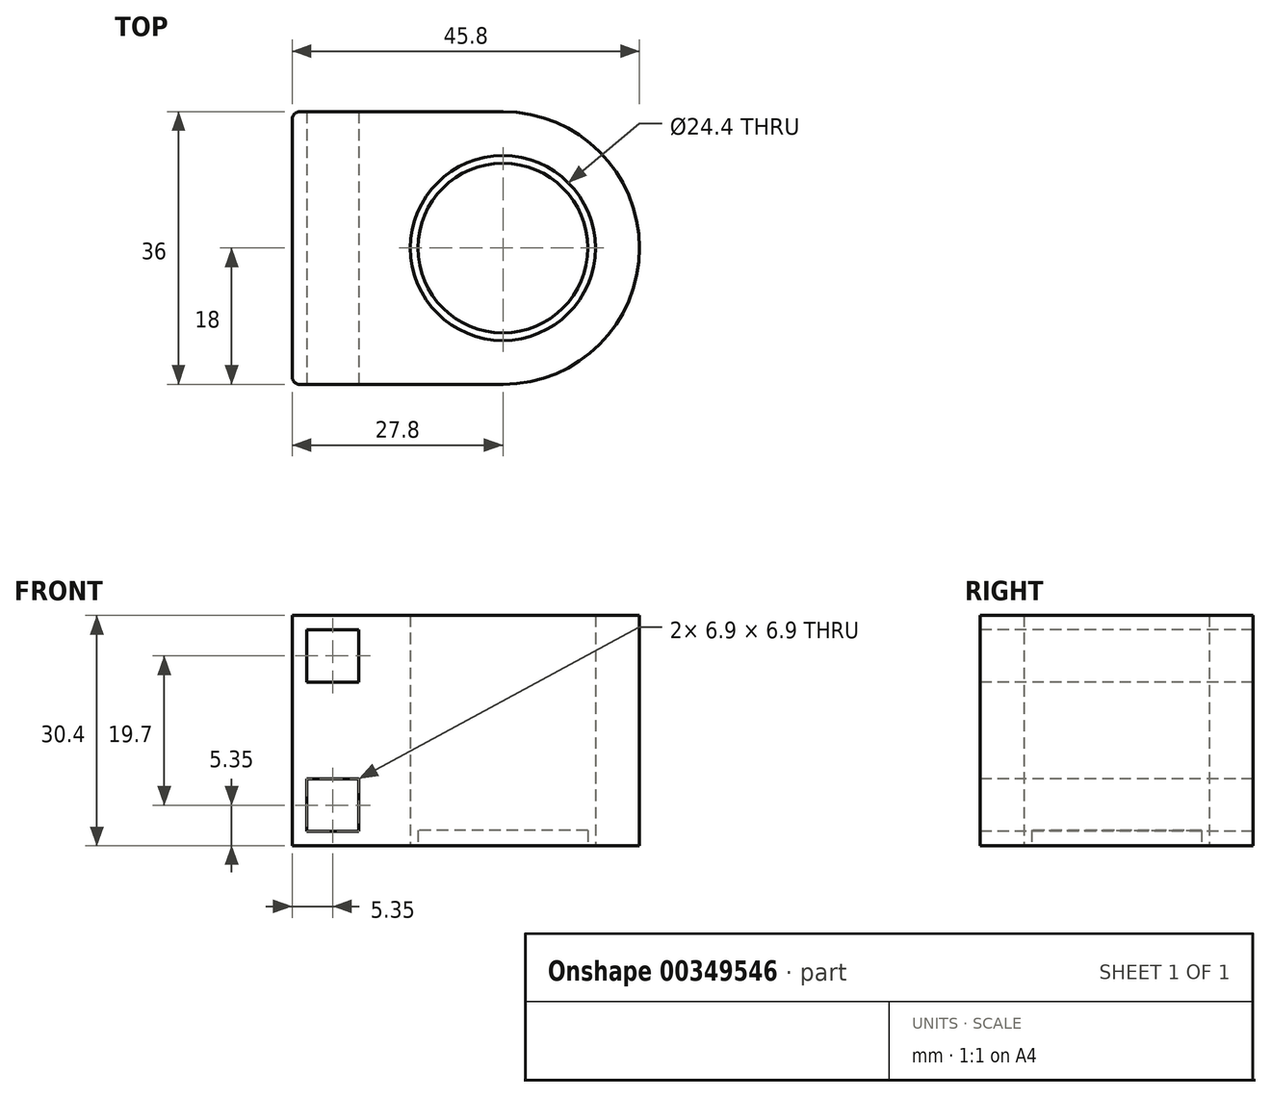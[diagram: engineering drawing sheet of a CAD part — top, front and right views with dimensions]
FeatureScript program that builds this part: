
annotation { "Feature Type Name" : "Feature", "Feature Type Description" : "" }
export const myFeature = defineFeature(function(context is Context, id is Id, definition is map)
    precondition{}
    {
        {
            var Q0;
            Q0=qCreatedBy(makeId("Top.planeOp"),FACE);
            var sketch = newSketch(context, id + "F0", { "sketchPlane" : qUnion([Q0])});
            skCircle(sketch, "E0", {"center": v(0, 0) * mm, "radius": 17.25 * mm});
            skCircle(sketch, "E1", {"center": v(0, 0) * mm, "radius": 18 * mm});
            skLineSegment(sketch, "E2", {"start": v(0, 0) * mm, "end": v(0, 18) * mm});
            skLineSegment(sketch, "E3.bottom", {"start": v(0, 18) * mm, "end": v(-27.8, 18) * mm});
            skLineSegment(sketch, "E3.top", {"start": v(0, -18) * mm, "end": v(-27.8, -18) * mm});
            skLineSegment(sketch, "E3.left", {"start": v(0, 18) * mm, "end": v(0, -18) * mm});
            skLineSegment(sketch, "E3.right", {"start": v(-27.8, 18) * mm, "end": v(-27.8, -18) * mm});
            skCircle(sketch, "E4", {"center": v(0, 0) * mm, "radius": 5 * mm});
            skCircle(sketch, "E5", {"center": v(0, 0) * mm, "radius": 11.2 * mm});
            skCircle(sketch, "E6", {"center": v(0, 0) * mm, "radius": 12.2 * mm});
            skSolve(sketch);
        }
        {
            var Q0;
            {var subQ1=sQuery(id+"F0.wireOp",EDGE,"E3.bottom");Q0=makeQuery(id+"F0.imprint","IMPRINT",FACE,{"disambiguationData":[TD([[makeQuery(id+"F0.imprint","IMPRINT",EDGE,{"derivedFrom":subQ1}),1.0]])]});}
            var Q1;
            {var subQ0=sQuery(id+"F0.wireOp",EDGE,"E3.left");var subQ1=sQuery(id+"F0.wireOp",EDGE,"E0");var subQ2=makeQuery(id+"F0.imprint","INTERSECT",VERTEX,{"disambiguationData":[OD(0.0)],"derivedFrom":[subQ1,subQ0]});Q1=makeQuery(id+"F0.imprint","IMPRINT",FACE,{"disambiguationData":[TD([[makeQuery(id+"F0.imprint","IMPRINT",EDGE,{"disambiguationData":[TD([[subQ2,-1.0]])],"derivedFrom":subQ1}),-1.0]])]});}
            var Q2;
            {var subQ0=sQuery(id+"F0.wireOp",EDGE,"E3.left");var subQ1=sQuery(id+"F0.wireOp",EDGE,"E0");var subQ2=makeQuery(id+"F0.imprint","INTERSECT",VERTEX,{"disambiguationData":[OD(0.0)],"derivedFrom":[subQ1,subQ0]});Q2=makeQuery(id+"F0.imprint","IMPRINT",FACE,{"disambiguationData":[TD([[makeQuery(id+"F0.imprint","IMPRINT",EDGE,{"disambiguationData":[TD([[subQ2,1.0]])],"derivedFrom":subQ1}),-1.0]])]});}
            extrude(context, id + "F1", {"entities" : qUnion([Q0, Q1, Q2]), "depth" : 30.4 * mm});
        }
        {
            var Q0;
            {var subQ5=sQuery(id+"F0.wireOp",EDGE,"E3.left");var subQ6=sQuery(id+"F0.wireOp",EDGE,"E0");var subQ7=makeQuery(id+"F0.imprint","INTERSECT",VERTEX,{"disambiguationData":[OD(0.0)],"derivedFrom":[subQ6,subQ5]});Q0=makeQuery(id+"F0.imprint","IMPRINT",FACE,{"disambiguationData":[TD([[makeQuery(id+"F0.imprint","IMPRINT",EDGE,{"disambiguationData":[TD([[subQ7,1.0]])],"derivedFrom":subQ6}),1.0]])]});}
            var Q1;
            {var subQ12=sQuery(id+"F0.wireOp",EDGE,"E3.left");var subQ13=sQuery(id+"F0.wireOp",EDGE,"E0");var subQ14=makeQuery(id+"F0.imprint","INTERSECT",VERTEX,{"disambiguationData":[OD(0.0)],"derivedFrom":[subQ13,subQ12]});Q1=makeQuery(id+"F0.imprint","IMPRINT",FACE,{"disambiguationData":[TD([[makeQuery(id+"F0.imprint","IMPRINT",EDGE,{"disambiguationData":[TD([[subQ14,-1.0]])],"derivedFrom":subQ13}),1.0]])]});}
            var Q2;
            {var subQ0=sQuery(id+"F0.wireOp",EDGE,"8lIcankL-Q5gj-hwWK-AL3X-qkDdrb8kB20Y");var subQ1=sQuery(id+"F0.wireOp",EDGE,"E3.left");var subQ2=makeQuery(id+"F0.imprint","INTERSECT",VERTEX,{"disambiguationData":[OD(1.0)],"derivedFrom":[subQ1,subQ0]});Q2=makeQuery(id+"F0.imprint","IMPRINT",FACE,{"disambiguationData":[TD([[makeQuery(id+"F0.imprint","IMPRINT",EDGE,{"disambiguationData":[TD([[subQ2,-1.0]])],"derivedFrom":subQ1}),-1.0]])]});}
            var Q3;
            {var subQ0=sQuery(id+"F0.wireOp",EDGE,"8lIcankL-Q5gj-hwWK-AL3X-qkDdrb8kB20Y");var subQ1=sQuery(id+"F0.wireOp",EDGE,"E3.left");var subQ2=makeQuery(id+"F0.imprint","INTERSECT",VERTEX,{"disambiguationData":[OD(1.0)],"derivedFrom":[subQ1,subQ0]});Q3=makeQuery(id+"F0.imprint","IMPRINT",FACE,{"disambiguationData":[TD([[makeQuery(id+"F0.imprint","IMPRINT",EDGE,{"disambiguationData":[TD([[subQ2,-1.0]])],"derivedFrom":subQ1}),1.0]])]});}
            var Q4;
            {var subQ0=sQuery(id+"F0.wireOp",EDGE,"acbbde6d-6b89-4c3b-ba40-6ba3c0975178.1");var subQ1=sQuery(id+"F0.wireOp",EDGE,"E4");var subQ2=makeQuery(id+"F0.imprint","INTERSECT",VERTEX,{"disambiguationData":[OD(1.0)],"derivedFrom":[subQ1,subQ0]});Q4=makeQuery(id+"F0.imprint","IMPRINT",FACE,{"disambiguationData":[TD([[makeQuery(id+"F0.imprint","IMPRINT",EDGE,{"disambiguationData":[TD([[subQ2,-1.0]])],"derivedFrom":subQ1}),-1.0]])]});}
            var Q5;
            {var subQ0=sQuery(id+"F0.wireOp",EDGE,"acbbde6d-6b89-4c3b-ba40-6ba3c0975178.2");var subQ1=sQuery(id+"F0.wireOp",EDGE,"E4");var subQ2=makeQuery(id+"F0.imprint","INTERSECT",VERTEX,{"disambiguationData":[OD(1.0)],"derivedFrom":[subQ1,subQ0]});Q5=makeQuery(id+"F0.imprint","IMPRINT",FACE,{"disambiguationData":[TD([[makeQuery(id+"F0.imprint","IMPRINT",EDGE,{"disambiguationData":[TD([[subQ2,1.0]])],"derivedFrom":subQ1}),-1.0]])]});}
            var Q6;
            {var subQ0=sQuery(id+"F0.wireOp",EDGE,"E4");var subQ1=sQuery(id+"F0.wireOp",EDGE,"E3.left");var subQ2=makeQuery(id+"F0.imprint","INTERSECT",VERTEX,{"disambiguationData":[OD(1.0)],"derivedFrom":[subQ1,subQ0]});Q6=makeQuery(id+"F0.imprint","IMPRINT",FACE,{"disambiguationData":[TD([[makeQuery(id+"F0.imprint","IMPRINT",EDGE,{"disambiguationData":[TD([[subQ2,-1.0]])],"derivedFrom":subQ1}),1.0]])]});}
            var Q7;
            {var subQ0=sQuery(id+"F0.wireOp",EDGE,"E4");var subQ1=sQuery(id+"F0.wireOp",EDGE,"E3.left");var subQ2=makeQuery(id+"F0.imprint","INTERSECT",VERTEX,{"disambiguationData":[OD(1.0)],"derivedFrom":[subQ1,subQ0]});Q7=makeQuery(id+"F0.imprint","IMPRINT",FACE,{"disambiguationData":[TD([[makeQuery(id+"F0.imprint","IMPRINT",EDGE,{"disambiguationData":[TD([[subQ2,-1.0]])],"derivedFrom":subQ1}),-1.0]])]});}
            extrude(context, id + "F2", {"entities" : qUnion([Q0, Q1, Q2, Q3, Q4, Q5, Q6, Q7]), "operationType" : NewBodyOperationType.ADD, "depth" : 2 * mm});
        }
        {
            var Q0;
            Q0=makeQuery(id+"F1.opExtrude","SWEPT_FACE",FACE,{"disambiguationData":[OSD([sQuery(id+"F0.wireOp",EDGE,"E3.top")])]});
            var sketch = newSketch(context, id + "F3", { "sketchPlane" : qUnion([Q0])});
            skLineSegment(sketch, "E7.bottom", {"start": v(-27.8, 30.4) * mm, "end": v(-25.9, 30.4) * mm});
            skLineSegment(sketch, "E7.top", {"start": v(-27.8, 28.5) * mm, "end": v(-25.9, 28.5) * mm});
            skLineSegment(sketch, "E7.left", {"start": v(-27.8, 30.4) * mm, "end": v(-27.8, 28.5) * mm});
            skLineSegment(sketch, "E7.right", {"start": v(-25.9, 30.4) * mm, "end": v(-25.9, 28.5) * mm});
            skLineSegment(sketch, "E8.bottom", {"start": v(-25.9, 28.5) * mm, "end": v(-19, 28.5) * mm});
            skLineSegment(sketch, "E8.top", {"start": v(-25.9, 21.6) * mm, "end": v(-19, 21.6) * mm});
            skLineSegment(sketch, "E8.left", {"start": v(-25.9, 28.5) * mm, "end": v(-25.9, 21.6) * mm});
            skLineSegment(sketch, "E8.right", {"start": v(-19, 28.5) * mm, "end": v(-19, 21.6) * mm});
            skPoint(sketch, "E9", {"position": v(-27.8, 15.2) * mm});
            skLineSegment(sketch, "E10", {"start": v(-27.8, 15.2) * mm, "end": v(0, 15.2) * mm});
            skLineSegment(sketch, "E11.MirrorCS", {"start": v(-25.9, 8.8) * mm, "end": v(-19, 8.8) * mm});
            skLineSegment(sketch, "E12.MirrorCS", {"start": v(-19, 1.9) * mm, "end": v(-19, 8.8) * mm});
            skLineSegment(sketch, "E13.MirrorCS", {"start": v(-25.9, 1.9) * mm, "end": v(-19, 1.9) * mm});
            skLineSegment(sketch, "E14.MirrorCS", {"start": v(-25.9, 1.9) * mm, "end": v(-25.9, 8.8) * mm});
            skSolve(sketch);
        }
        {
            var Q0;
            Q0=makeQuery(id+"F3.imprint","IMPRINT",FACE,{"disambiguationData":[TD([[makeQuery(id+"F3.imprint","IMPRINT",EDGE,{"derivedFrom":sQuery(id+"F3.wireOp",EDGE,"E8.bottom")}),-1.0]])]});
            var Q1;
            Q1=makeQuery(id+"F3.imprint","IMPRINT",FACE,{"disambiguationData":[TD([[makeQuery(id+"F3.imprint","IMPRINT",EDGE,{"derivedFrom":sQuery(id+"F3.wireOp",EDGE,"E11.MirrorCS")}),-1.0]])]});
            extrude(context, id + "F4", {"entities" : qUnion([Q0, Q1]), "operationType" : NewBodyOperationType.REMOVE, "oppositeDirection" : true, "depth" : 50 * mm});
        }
        {
            var Q0;
            Q0=makeQuery(id+"F1.opExtrude","SWEPT_EDGE",EDGE,{"disambiguationData":[OSD([sQuery(id+"F0.wireOp",EDGE,"E3.bottom"),sQuery(id+"F0.wireOp",EDGE,"E3.right")])]});
            var Q1;
            Q1=makeQuery(id+"F1.opExtrude","SWEPT_EDGE",EDGE,{"disambiguationData":[OSD([sQuery(id+"F0.wireOp",EDGE,"E3.top"),sQuery(id+"F0.wireOp",EDGE,"E3.right")])]});
            fillet(context, id + "F5", {"entities" : qUnion([Q0, Q1]), "radius" : 1 * mm, "tangentPropagation" : true, "allowEdgeOverflow" : false});
        }
        {
            var Q0;
            {var subQ0=sQuery(id+"F0.wireOp",EDGE,"E6");var subQ1=sQuery(id+"F0.wireOp",EDGE,"E3.left");var subQ2=makeQuery(id+"F0.imprint","INTERSECT",VERTEX,{"disambiguationData":[OD(0.0)],"derivedFrom":[subQ1,subQ0]});Q0=makeQuery(id+"F0.imprint","IMPRINT",FACE,{"disambiguationData":[TD([[makeQuery(id+"F0.imprint","IMPRINT",EDGE,{"disambiguationData":[TD([[subQ2,-1.0]])],"derivedFrom":subQ1}),-1.0]])]});}
            var Q1;
            {var subQ0=sQuery(id+"F0.wireOp",EDGE,"E6");var subQ1=sQuery(id+"F0.wireOp",EDGE,"E3.left");var subQ2=makeQuery(id+"F0.imprint","INTERSECT",VERTEX,{"disambiguationData":[OD(0.0)],"derivedFrom":[subQ1,subQ0]});Q1=makeQuery(id+"F0.imprint","IMPRINT",FACE,{"disambiguationData":[TD([[makeQuery(id+"F0.imprint","IMPRINT",EDGE,{"disambiguationData":[TD([[subQ2,-1.0]])],"derivedFrom":subQ1}),1.0]])]});}
            var Q2;
            Q2=makeQuery(id+"F1.opExtrude","CAP_FACE",FACE,{"disambiguationData":[OSD([sQuery(id+"F0.wireOp",EDGE,"E0"),sQuery(id+"F0.wireOp",EDGE,"E1"),sQuery(id+"F0.wireOp",EDGE,"E3.bottom"),sQuery(id+"F0.wireOp",EDGE,"E3.top"),sQuery(id+"F0.wireOp",EDGE,"E3.right")])],"isStart":false});
            extrude(context, id + "F6", {"entities" : qUnion([Q0, Q1]), "operationType" : NewBodyOperationType.ADD, "endBound" : BoundingType.UP_TO_SURFACE, "endBoundEntityFace" : qUnion([Q2]), "depth" : 25 * mm});
        }
    });
